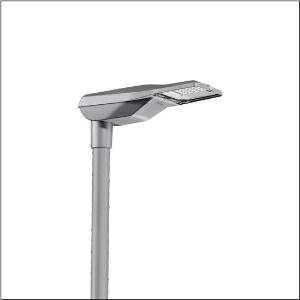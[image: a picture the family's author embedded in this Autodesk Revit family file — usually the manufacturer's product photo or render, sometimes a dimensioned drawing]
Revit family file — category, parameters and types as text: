
# Revit family: streetlight_sl_21_iq_micro___st1_0a_5xe1d41g08cb_d625
name_source: partatom
category: Lighting Fixtures
units: mm (PartAtom-declared; Revit-internal decimal feet)

## family parameters
Cut with Voids When Loaded = No
Host = Face
Light Source = No
Part Type = Normal
Room Calculation Point = No
Round Connector Dimension = Use Diameter
Shared = No

## types (1)
- --- (1 x LED, 2980 lm, 19.4 W, 4000K)
    Apparent Load = 19 VA
    CIE Flux Codes = 37 72 97 100 100
    Color Rendering = 70
    Color Temperature = 4000K
    Default Elevation = 1800 mm
    Description = Streetlight SL 21 iQ micro, mast luminaire, primary light control with lens, of PMMA, primary optical cover: cover, of toughened safety glass, transparent, light distribution: ST1.0a, light emission: direct distribution, primary light characteristic: asymmetric, installation type: post-top, side-entry, LED, High Power LED, rated luminous flux: 2.980lm, luminous efficacy: 154lm/W, light colour: 740, colour temperature: 4000K, control: Street-Remote, Auto-Match, Temp-Guard, Lumen-Switch, Night-Set, Smart-Wire, Light-Fading, Desk-Remote (wireless, voltage-free reading and setting of iQ features in the workshop via application-optimized NFC function/RFID function), optimised constant luminous flux control (CLO 2.0), pre-setting: linear dimming characteristic, mains connection: 220..240V, AC, 50/60Hz, start of lifetime: 19W, end of service life: 20W, reduction: 10W, luminaire housing, of diecast aluminium, powder-coated, Siteco® metallic grey (DB 702S), corrosivity category C5 mid according to DIN EN ISO 12944, please order mast flange separately, inclination adjustable: 0°, 5°, 10°, 15°, sealing non-destructively replaceable, multi-level sealing system, length: 528mm, width: 235mm, height: 110mm, mast flange for spigot size: 42mm (side-entry): 5XC10008XM4, 60/48mm (side-entry/post-top): 5XC10108XM2, 76/60mm (side-entry/post-top): 5XC10108XM1, protection rating (complete): IP66, insulation class (complete): insulation class II (safety insulation), certification: CE, ENEC, ENEC+, VDE, impact resistance: IK09, permissible operating ambient temperature for outdoor applications: -40..+50°C, standard-compliant lighting for roads and squares, packaging unit: 1 piece

Light Distribution: ST1.0a
    Height = 110 mm
    Lamp = 1 x LED
    Lamp Light Flux = 2980 lm
    Lamp Power = 19.4 W
    Lamp count = 1
    Length = 528 mm
    Luminous efficacy = 154 lm/W
    Manufacturer = Siteco
    ModVariant = No
    Model = 5XE1D41G08CB
    Number of Poles = 1
    OnlyDefault = Yes
    Power Factor = 1
    Product Name = Streetlight SL 21 iQ micro | ST1.0a
    Product group = mast luminaire | pylon top
    ProductGroupID = 6100
    Protection Class = Protection class II
    Protection Degree = IP 66
    RLX_Detail_Level = 1
    RLX_Emergency_Light_Flux = 0 lm
    RLX_Emergency_Type = 0
    RLX_Emergency_Type_DB = No
    RlxData = <blob elided: 98533 chars, md5=b2ae40c0>
    Socket = socket
    Standby Power = 0 W
    System Light Flux = 2980 lm
    System Power = 19 W
    Type Comments = factory setting: luminous flux: 100 % | dim-lin: 254 | 387 mA
    Type Image = l_1006881.jpg
    URL = http://relux.com
    VarID = @adj_108983
    Voltage = 0 V
    Weight = 0.00 kg
    Width = 235 mm

## geometry (parser evidence)
native form markers: Blend x4, Sweep x10
no freeform markers — native parametric forms only
